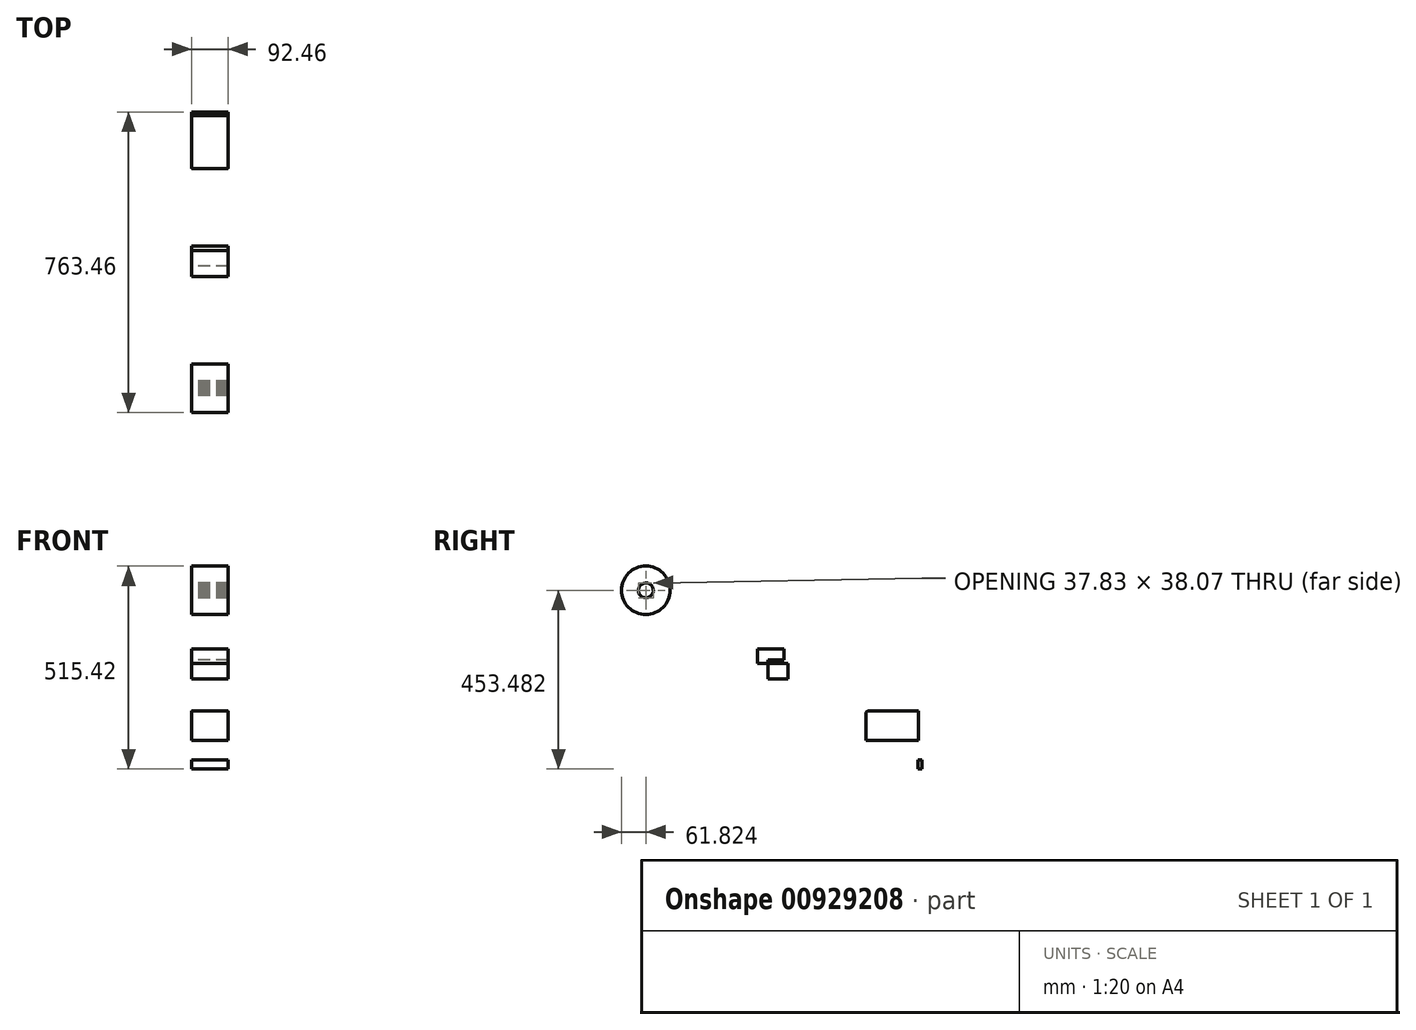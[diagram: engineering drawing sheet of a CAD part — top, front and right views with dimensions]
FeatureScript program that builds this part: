
annotation { "Feature Type Name" : "Feature", "Feature Type Description" : "" }
export const myFeature = defineFeature(function(context is Context, id is Id, definition is map)
    precondition{}
    {
        {
            var Q0;
            Q0=qCreatedBy(makeId("Right.planeOp"),FACE);
            var sketch = newSketch(context, id + "F0", { "sketchPlane" : qUnion([Q0])});
            skLineSegment(sketch, "E0.bottom", {"start": v(-19.1, 21.73) * mm, "end": v(31.15, 21.73) * mm});
            skLineSegment(sketch, "E0.top", {"start": v(-19.1, -17.32) * mm, "end": v(31.15, -17.32) * mm});
            skLineSegment(sketch, "E0.left", {"start": v(-19.1, 21.73) * mm, "end": v(-19.1, -17.32) * mm});
            skLineSegment(sketch, "E0.right", {"start": v(31.15, 21.73) * mm, "end": v(31.15, -17.32) * mm});
            skLineSegment(sketch, "E1.bottom", {"start": v(20.42, 30.99) * mm, "end": v(-45.93, 30.99) * mm});
            skLineSegment(sketch, "E1.top", {"start": v(20.42, 59.15) * mm, "end": v(-45.93, 59.15) * mm});
            skLineSegment(sketch, "E1.left", {"start": v(20.42, 30.99) * mm, "end": v(20.42, 59.15) * mm});
            skLineSegment(sketch, "E1.right", {"start": v(-45.93, 30.99) * mm, "end": v(-45.93, 59.15) * mm});
            skLineSegment(sketch, "E2.bottom", {"start": v(-45.93, 59.15) * mm, "end": v(-19.1, 59.15) * mm});
            skLineSegment(sketch, "E2.top", {"start": v(-45.93, 21.73) * mm, "end": v(-19.1, 21.73) * mm});
            skLineSegment(sketch, "E2.left", {"start": v(-45.93, 59.15) * mm, "end": v(-45.93, 21.73) * mm});
            skLineSegment(sketch, "E2.right", {"start": v(-19.1, 59.15) * mm, "end": v(-19.1, 21.73) * mm});
            skLineSegment(sketch, "E3.bottom", {"start": v(363, -173.75) * mm, "end": v(228.71, -173.75) * mm});
            skLineSegment(sketch, "E3.top", {"start": v(363, -99.2) * mm, "end": v(235.06, -99.2) * mm});
            skLineSegment(sketch, "E3.left", {"start": v(363, -173.75) * mm, "end": v(363, -99.2) * mm});
            skLineSegment(sketch, "E3.right", {"start": v(228.71, -173.75) * mm, "end": v(228.71, -105.55) * mm});
            skLineSegment(sketch, "E4.bottom", {"start": v(361.65, -245.93) * mm, "end": v(371.77, -245.93) * mm});
            skLineSegment(sketch, "E4.top", {"start": v(361.65, -223.33) * mm, "end": v(371.77, -223.33) * mm});
            skLineSegment(sketch, "E4.left", {"start": v(361.65, -245.93) * mm, "end": v(361.65, -223.33) * mm});
            skLineSegment(sketch, "E4.right", {"start": v(371.77, -245.93) * mm, "end": v(371.77, -223.33) * mm});
            skCircle(sketch, "E5", {"center": v(-330.02, 207.82) * mm, "radius": 61.67 * mm});
            skCircle(sketch, "E6.cCircle", {"center": v(-329.87, 207.55) * mm, "radius": 18.85 * mm, "construction": true});
            skLineSegment(sketch, "E6.0", {"start": v(-348.78, 209.76) * mm, "end": v(-347.4, 215) * mm});
            skLineSegment(sketch, "E6.1", {"start": v(-347.4, 215) * mm, "end": v(-344.58, 219.63) * mm});
            skLineSegment(sketch, "E6.2", {"start": v(-344.58, 219.63) * mm, "end": v(-340.58, 223.29) * mm});
            skLineSegment(sketch, "E6.3", {"start": v(-340.58, 223.29) * mm, "end": v(-335.72, 225.67) * mm});
            skLineSegment(sketch, "E6.4", {"start": v(-335.72, 225.67) * mm, "end": v(-330.38, 226.59) * mm});
            skLineSegment(sketch, "E6.5", {"start": v(-330.38, 226.59) * mm, "end": v(-325, 225.96) * mm});
            skLineSegment(sketch, "E6.6", {"start": v(-325, 225.96) * mm, "end": v(-320, 223.84) * mm});
            skLineSegment(sketch, "E6.7", {"start": v(-320, 223.84) * mm, "end": v(-315.81, 220.4) * mm});
            skLineSegment(sketch, "E6.8", {"start": v(-315.81, 220.4) * mm, "end": v(-312.76, 215.92) * mm});
            skLineSegment(sketch, "E6.9", {"start": v(-312.76, 215.92) * mm, "end": v(-311.1, 210.77) * mm});
            skLineSegment(sketch, "E6.10", {"start": v(-311.1, 210.77) * mm, "end": v(-310.95, 205.35) * mm});
            skLineSegment(sketch, "E6.11", {"start": v(-310.95, 205.35) * mm, "end": v(-312.34, 200.1) * mm});
            skLineSegment(sketch, "E6.12", {"start": v(-312.34, 200.1) * mm, "end": v(-315.15, 195.47) * mm});
            skLineSegment(sketch, "E6.13", {"start": v(-315.15, 195.47) * mm, "end": v(-319.15, 191.81) * mm});
            skLineSegment(sketch, "E6.14", {"start": v(-319.15, 191.81) * mm, "end": v(-324.01, 189.43) * mm});
            skLineSegment(sketch, "E6.15", {"start": v(-324.01, 189.43) * mm, "end": v(-329.36, 188.52) * mm});
            skLineSegment(sketch, "E6.16", {"start": v(-329.36, 188.52) * mm, "end": v(-334.74, 189.15) * mm});
            skLineSegment(sketch, "E6.17", {"start": v(-334.74, 189.15) * mm, "end": v(-339.73, 191.26) * mm});
            skLineSegment(sketch, "E6.18", {"start": v(-339.73, 191.26) * mm, "end": v(-343.92, 194.7) * mm});
            skLineSegment(sketch, "E6.19", {"start": v(-343.92, 194.7) * mm, "end": v(-346.97, 199.18) * mm});
            skLineSegment(sketch, "E6.20", {"start": v(-346.97, 199.18) * mm, "end": v(-348.63, 204.34) * mm});
            skLineSegment(sketch, "E6.21", {"start": v(-348.63, 204.34) * mm, "end": v(-348.78, 209.76) * mm});
            skPoint(sketch, "E6.0.midPoint", {"position": v(-348.09, 212.38) * mm});
            skPoint(sketch, "E7.visualSharp", {"position": v(228.71, -99.2) * mm});
            skArc(sketch, "E7.filletArc", {"start": v(235.06, -99.2) * mm, "mid": v(230.57, -101.06) * mm, "end": v(228.71, -105.55) * mm});
            skLineSegment(sketch, "E8.0", {"start": v(397.29, -173.75) * mm, "end": v(397.29, -99.2) * mm});
            skLineSegment(sketch, "E9.0", {"start": v(390.94, -173.75) * mm, "end": v(390.94, -99.2) * mm});
            skLineSegment(sketch, "E10.0", {"start": v(359.14, -173.75) * mm, "end": v(359.14, -99.2) * mm});
            skLineSegment(sketch, "E11.MirrorCS", {"start": v(403.64, -173.75) * mm, "end": v(403.64, -99.2) * mm});
            skSolve(sketch);
        }
        {
            var Q0;
            Q0 = qSketchRegion(id + "F0", true);
            extrude(context, id + "F1", {"entities" : qUnion([Q0]), "depth" : 92.46 * mm, "offsetDistance" : 25.4 * mm});
        }
    });
